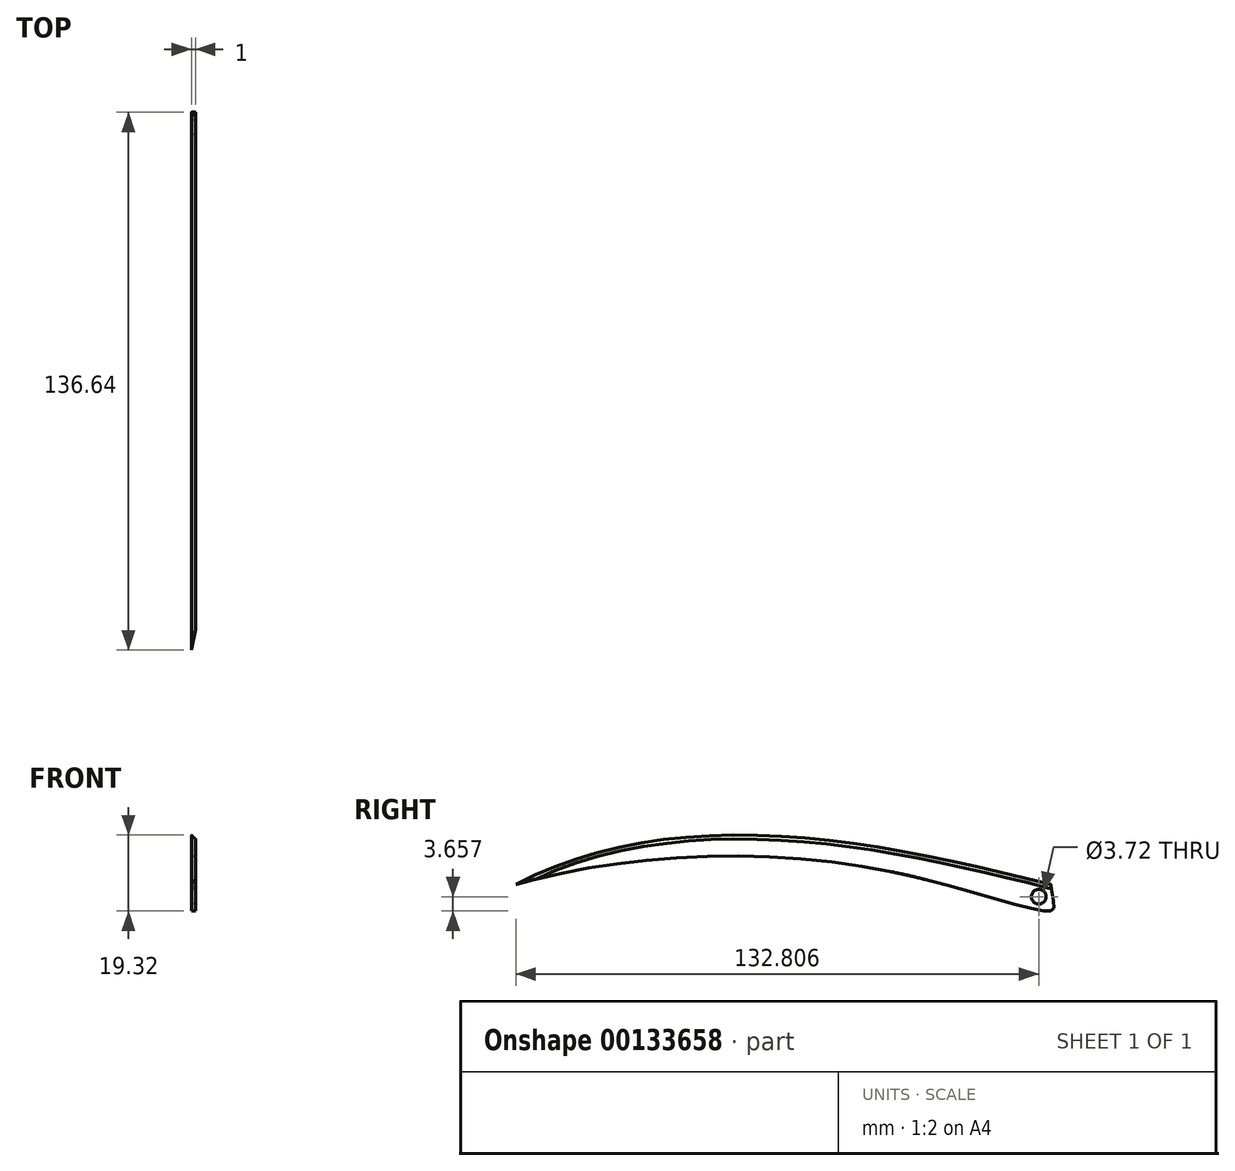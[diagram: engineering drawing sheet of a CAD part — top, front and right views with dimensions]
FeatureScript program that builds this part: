
annotation { "Feature Type Name" : "Feature", "Feature Type Description" : "" }
export const myFeature = defineFeature(function(context is Context, id is Id, definition is map)
    precondition{}
    {
        {
            var Q0;
            Q0=qCreatedBy(makeId("Right.planeOp"),FACE);
            var sketch = newSketch(context, id + "F0", { "sketchPlane" : qUnion([Q0])});
            skFitSpline(sketch, "E0", {"points": [v(0, 0) * mm, v(-74.77, 12.53) * mm, v(-135.84, 0) * mm], "startDerivative": vector(-146.28, 37.06) * mm, "endDerivative": vector(-112.08, -60.4) * mm});
            skFitSpline(sketch, "E1", {"points": [v(-135.84, 0) * mm, v(-45.9, 4.31) * mm, v(0, -6.65) * mm, v(0, 0) * mm], "startDerivative": vector(145.55, 43.13) * mm, "endDerivative": vector(-13.5, 101.41) * mm});
            skPoint(sketch, "E2", {"position": v(-3.03, -3.08) * mm});
            skCircle(sketch, "E3", {"center": v(-3.03, -3.08) * mm, "radius": 1.86 * mm});
            skSolve(sketch);
        }
        {
            var Q0;
            Q0=makeQuery(id+"F0.imprint","IMPRINT",FACE,{"disambiguationData":[TD([[makeQuery(id+"F0.imprint","IMPRINT",EDGE,{"derivedFrom":sQuery(id+"F0.wireOp",EDGE,"E0")}),1.0]])]});
            extrude(context, id + "F1", {"entities" : qUnion([Q0]), "endBound" : BoundingType.SYMMETRIC, "depth" : 1 * mm});
        }
        {
            var Q0;
            Q0=makeQuery(id+"F1.opExtrude","CAP_EDGE",EDGE,{"disambiguationData":[OSD([sQuery(id+"F0.wireOp",EDGE,"E0")])],"isStart":false});
            chamfer(context, id + "F2", {"entities" : qUnion([Q0]), "width" : 1 * mm, "tangentPropagation" : true});
        }
    });
